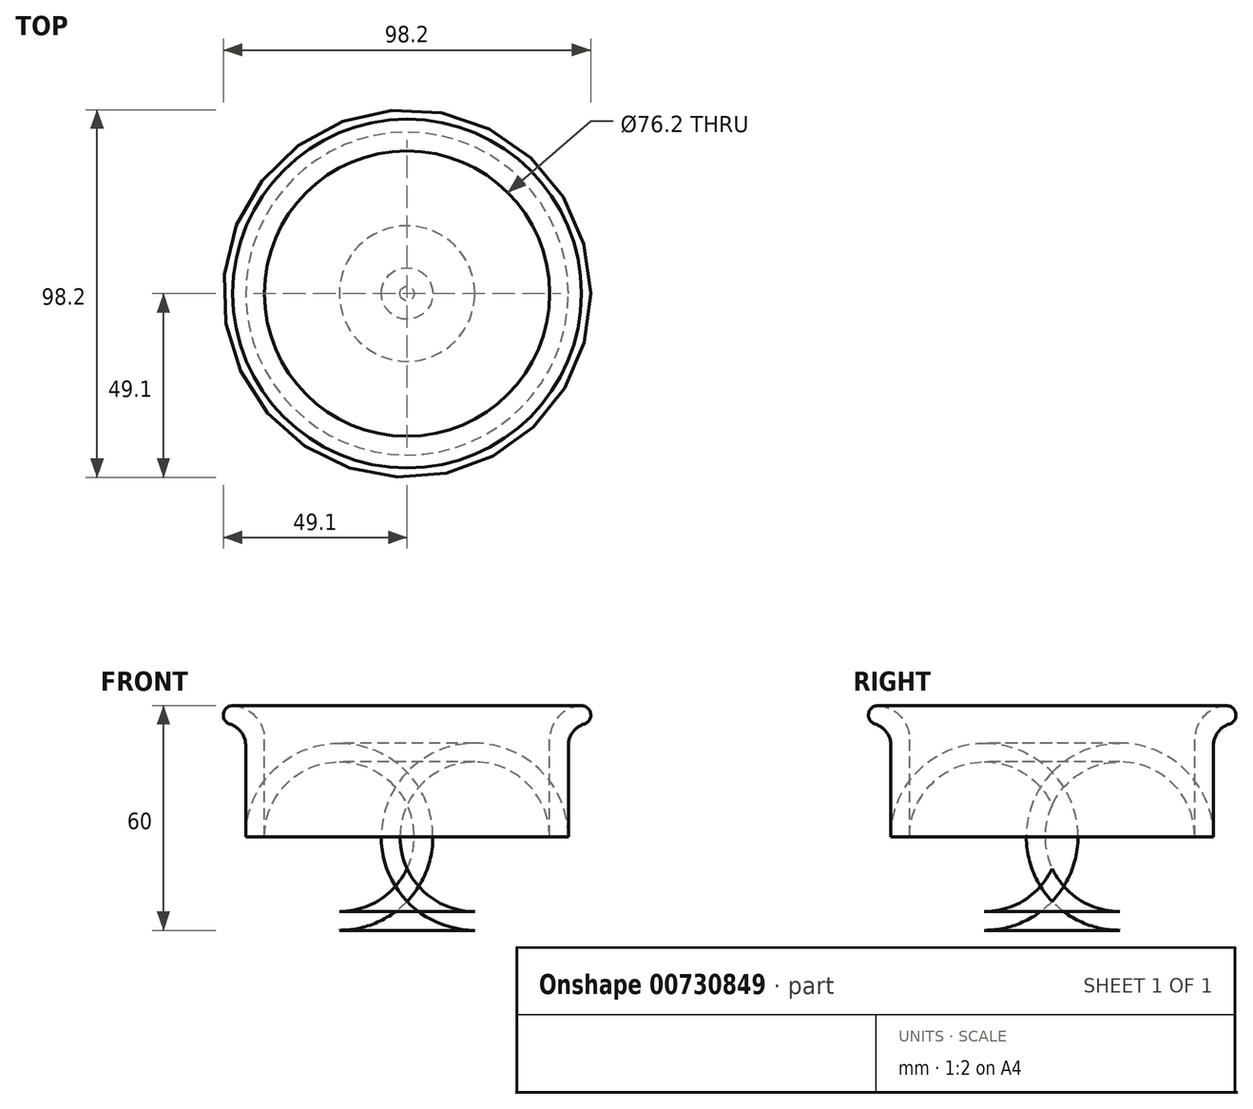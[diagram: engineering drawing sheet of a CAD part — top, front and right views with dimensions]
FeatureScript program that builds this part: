
annotation { "Feature Type Name" : "Feature", "Feature Type Description" : "" }
export const myFeature = defineFeature(function(context is Context, id is Id, definition is map)
    precondition{}
    {
        {
            var Q0;
            Q0=qCreatedBy(makeId("Front.planeOp"),FACE);
            var sketch = newSketch(context, id + "F0", { "sketchPlane" : qUnion([Q0])});
            skLineSegment(sketch, "E0", {"start": v(0, 56.07) * mm, "end": v(0, -56.2) * mm});
            skSolve(sketch);
        }
        {
            var Q0;
            Q0=qCreatedBy(makeId("Front.planeOp"),FACE);
            var sketch = newSketch(context, id + "F1", { "sketchPlane" : qUnion([Q0])});
            skLineSegment(sketch, "E1", {"start": v(49.1, 35.97) * mm, "end": v(49.1, 40.97) * mm});
            skLineSegment(sketch, "E2", {"start": v(49.1, 40.97) * mm, "end": v(38.1, 40.97) * mm});
            skLineSegment(sketch, "E3", {"start": v(38.1, 40.97) * mm, "end": v(38.1, 5.97) * mm});
            skLineSegment(sketch, "E4", {"start": v(18.1, -14.03) * mm, "end": v(0, -14.03) * mm});
            skLineSegment(sketch, "E5", {"start": v(0, -14.03) * mm, "end": v(0, -19.03) * mm});
            skLineSegment(sketch, "E6", {"start": v(0, -19.03) * mm, "end": v(18.1, -19.03) * mm});
            skLineSegment(sketch, "E7", {"start": v(43.1, 5.97) * mm, "end": v(43.1, 35.97) * mm});
            skLineSegment(sketch, "E8", {"start": v(43.1, 35.97) * mm, "end": v(49.1, 35.97) * mm});
            skPoint(sketch, "E9.visualSharp", {"position": v(43.1, -19.03) * mm});
            skArc(sketch, "E9.filletArc", {"start": v(18.1, -19.03) * mm, "mid": v(35.78, -11.71) * mm, "end": v(43.1, 5.97) * mm});
            skPoint(sketch, "E10.visualSharp", {"position": v(38.1, -14.03) * mm});
            skArc(sketch, "E10.filletArc", {"start": v(18.1, -14.03) * mm, "mid": v(32.24, -8.18) * mm, "end": v(38.1, 5.97) * mm});
            skSolve(sketch);
        }
        {
            var Q0;
            Q0 = qSketchRegion(id + "F1", true);
            var Q1;
            Q1=sQuery(id+"F0.wireOp",EDGE,"E0");
            revolve(context, id + "F2", {"surfaceOperationType" : NewSurfaceOperationType.NEW, "entities" : qUnion([Q0]), "axis" : qUnion([Q1]), "revolveType" : RevolveType.FULL});
        }
        {
            var Q0;
            Q0=makeQuery(id+"F2.opRevolve","SWEPT_EDGE",EDGE,{"disambiguationData":[OSD([sQuery(id+"F1.wireOp",EDGE,"E1"),sQuery(id+"F1.wireOp",EDGE,"E8")])]});
            var Q1;
            Q1=makeQuery(id+"F2.opRevolve","SWEPT_EDGE",EDGE,{"disambiguationData":[OSD([sQuery(id+"F1.wireOp",EDGE,"E1"),sQuery(id+"F1.wireOp",EDGE,"E2")])]});
            fillet(context, id + "F3", {"entities" : qUnion([Q0, Q1]), "radius" : 2.5 * mm, "tangentPropagation" : true, "allowEdgeOverflow" : false});
        }
        {
            var Q0;
            Q0=makeQuery(id+"F2.opRevolve","SWEPT_EDGE",EDGE,{"disambiguationData":[OSD([sQuery(id+"F1.wireOp",EDGE,"E6"),sQuery(id+"F1.wireOp",EDGE,"E7")])]});
            fillet(context, id + "F4", {"entities" : qUnion([Q0]), "radius" : 6 * mm, "tangentPropagation" : true, "allowEdgeOverflow" : false});
        }
        {
            var Q0;
            Q0=makeQuery(id+"F2.opRevolve","SWEPT_EDGE",EDGE,{"disambiguationData":[OSD([sQuery(id+"F1.wireOp",EDGE,"E2"),sQuery(id+"F1.wireOp",EDGE,"E3")])]});
            fillet(context, id + "F5", {"entities" : qUnion([Q0]), "radius" : 9 * mm, "tangentPropagation" : true, "allowEdgeOverflow" : false});
        }
    });
